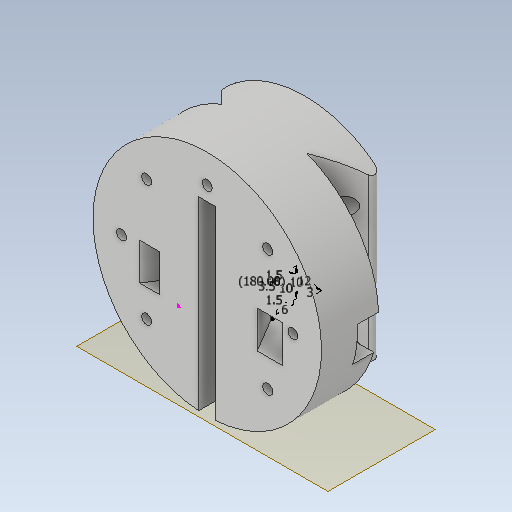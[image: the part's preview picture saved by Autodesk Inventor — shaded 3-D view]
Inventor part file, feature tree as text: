
AUTODESK INVENTOR PART (.ipt)
format: ipt  version: 2020.1 (Build 241239000, 239)  size: 366,080 bytes
history: native  units: mm
features: sketch x13, extrude x9, loft x2, other x2, mirror x1, fillet x1, plane x1
ambient origin geometry x8: Origin, YZ Plane, XZ Plane, XY Plane, X Axis, Y Axis, Z Axis, Center Point
bodies: Solid1 (feature_tree)
feature tree (29):
  extrude  "base"  Depth=20.0mm TaperAngle=0.0deg
  extrude  "tail_horse_1"  Depth=20.0mm
  mirror  "tail_horse_2"
  fillet  "fillet_tail_horse"  [1 undecoded]
  extrude  "attach_screw"  Depth=20.0mm
  extrude  "attach_screw_head"  Depth=20.0mm TaperAngle=0.0deg
  extrude  "lock_arm"  Depth=2.0mm
  plane  "Work Plane1"
  extrude  "servo_place"  Depth=3.5mm TaperAngle=360.0deg
  sketch  "Sketch7"  dims[d18=0.0mm d19=0.0mm d20=30.0mm]
  sketch  "Sketch8"  dims[d21=6.0mm d22=80.0mm d24=360.0deg]
  sketch  "Sketch9"  dims[d26=20.0mm d27=0.0mm d28=8.0mm]
  extrude  "Extrusion8"  Depth=30.0mm
  extrude  "Extrusion9"  Depth=80.0mm TaperAngle=360.0deg
  sketch  "Sketch12"  dims[d32=10.0mm d33=25.0mm]
  sketch  "Sketch13"  dims[d34=20.0mm]
  loft  "Loft1"
  loft  "Loft3"
  extrude  "holgura"  Depth=25.0mm
  sketch  "Sketch1"  dims[d0=80.0mm d1=20.0mm d2=0.0mm]
  sketch  "Sketch2"  dims[d3=15.0mm d4=20.0mm d5=135.0deg]
  sketch  "Sketch3"  dims[d6=15.0mm d7=20.0mm]
  sketch  "Sketch4"  dims[d8=135.0deg d9=20.0mm d10=0.0mm]
  sketch  "Sketch5"  dims[d11=2.0mm d12=30.0mm]
  sketch  "Sketch6"  dims[d13=3.5mm d14=80.0mm d16=360.0deg]
  sketch  "Sketch11"  dims[d29=3.5mm d30=0.0mm d31=0.0mm]
  other  "Edges1"
  other  "Edges4"
  sketch  "Sketch14"  dims[d35=65.0mm d36=0.0mm d37=6.0mm d38=2.0mm d39=3.0mm d40=6.0mm d41=3.0mm d42=3.5mm d43=180.0deg d44=1.5mm d46=10.0mm d47=6.0mm d48=10.0mm d49=1.5mm d50=12.0mm d51=11.5mm d52=4.5mm d53=13.0mm d54=9.0mm d55=13.0mm d56=90.0deg d57=8.0mm d58=12.0mm d59=3.0mm d64=10.0mm d65=0.0mm d74=80.0mm d75=8.5mm d76=11.5mm d77=5.5mm d78=11.5mm d79=5.5mm d80=10.0mm d81=0.0mm d82=7.0mm d83=0.0mm d84=90.0deg d85=0.0mm d86=90.0deg d93=0.0mm d94=90.0deg d95=0.0mm d96=90.0deg d97=0.5mm d98=57.0mm d99=21.0mm d100=10.0mm d101=10.0mm d102=0.0mm]
note: 1 required parameter value undecoded (feature->parameter linkage not recoverable at this tier; creation-order binding heuristic only, values carry confidence <= 0.55)
